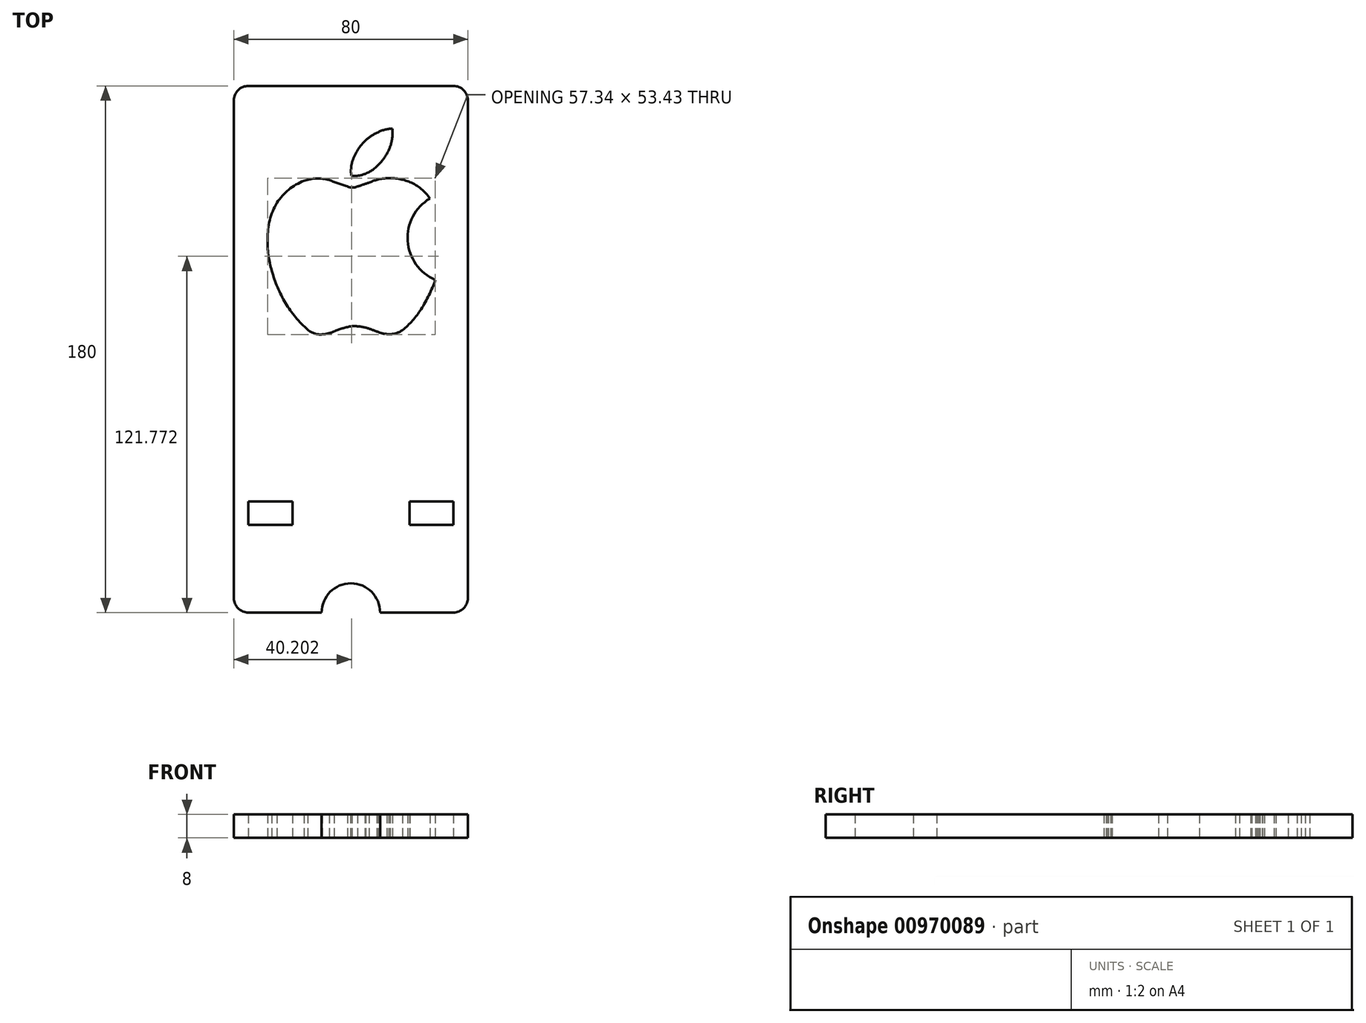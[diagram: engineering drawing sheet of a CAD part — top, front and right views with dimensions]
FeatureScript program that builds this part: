
annotation { "Feature Type Name" : "Feature", "Feature Type Description" : "" }
export const myFeature = defineFeature(function(context is Context, id is Id, definition is map)
    precondition{}
    {
        {
            var Q0;
            Q0=qCreatedBy(makeId("Top.planeOp"),FACE);
            var sketch = newSketch(context, id + "F0", { "sketchPlane" : qUnion([Q0])});
            skLineSegment(sketch, "E0.bottom", {"start": v(-35, 90) * mm, "end": v(35, 90) * mm});
            skLineSegment(sketch, "E0.top", {"start": v(-35, -90) * mm, "end": v(-10, -90) * mm});
            skLineSegment(sketch, "E0.left", {"start": v(-40, 85) * mm, "end": v(-40, -85) * mm});
            skLineSegment(sketch, "E0.right", {"start": v(40, 85) * mm, "end": v(40, -85) * mm});
            skArc(sketch, "E1", {"start": v(-10, -90) * mm, "mid": v(0, -80) * mm, "end": v(10, -90) * mm});
            skLineSegment(sketch, "E2.trimOffspring", {"start": v(10, -90) * mm, "end": v(35, -90) * mm});
            skPoint(sketch, "E3.visualSharp", {"position": v(40, 90) * mm});
            skArc(sketch, "E3.filletArc", {"start": v(40, 85) * mm, "mid": v(38.54, 88.54) * mm, "end": v(35, 90) * mm});
            skPoint(sketch, "E4.visualSharp", {"position": v(-40, 90) * mm});
            skArc(sketch, "E4.filletArc", {"start": v(-35, 90) * mm, "mid": v(-38.54, 88.54) * mm, "end": v(-40, 85) * mm});
            skPoint(sketch, "E5.visualSharp", {"position": v(40, -90) * mm});
            skArc(sketch, "E5.filletArc", {"start": v(35, -90) * mm, "mid": v(38.54, -88.54) * mm, "end": v(40, -85) * mm});
            skPoint(sketch, "E6.visualSharp", {"position": v(-40, -90) * mm});
            skArc(sketch, "E6.filletArc", {"start": v(-40, -85) * mm, "mid": v(-38.54, -88.54) * mm, "end": v(-35, -90) * mm});
            skLineSegment(sketch, "E7.bottom", {"start": v(-35, -52) * mm, "end": v(-20, -52) * mm});
            skLineSegment(sketch, "E7.top", {"start": v(-35, -60) * mm, "end": v(-20, -60) * mm});
            skLineSegment(sketch, "E7.left", {"start": v(-35, -52) * mm, "end": v(-35, -60) * mm});
            skLineSegment(sketch, "E7.right", {"start": v(-20, -52) * mm, "end": v(-20, -60) * mm});
            skLineSegment(sketch, "E8.bottom", {"start": v(20, -52) * mm, "end": v(35, -52) * mm});
            skLineSegment(sketch, "E8.top", {"start": v(20, -60) * mm, "end": v(35, -60) * mm});
            skLineSegment(sketch, "E8.left", {"start": v(20, -52) * mm, "end": v(20, -60) * mm});
            skLineSegment(sketch, "E8.right", {"start": v(35, -52) * mm, "end": v(35, -60) * mm});
            skArc(sketch, "E9", {"start": v(-16.02, 57.55) * mm, "mid": v(-21.25, 54.54) * mm, "end": v(-25.26, 50.04) * mm});
            skArc(sketch, "E10", {"start": v(-25.26, 50.04) * mm, "mid": v(-27.73, 44.1) * mm, "end": v(-28.45, 37.72) * mm});
            skArc(sketch, "E11", {"start": v(-28.45, 37.72) * mm, "mid": v(-28.19, 32.2) * mm, "end": v(-27.02, 26.8) * mm});
            skArc(sketch, "E12", {"start": v(-27.02, 26.8) * mm, "mid": v(-25.06, 21.15) * mm, "end": v(-22.35, 15.82) * mm});
            skArc(sketch, "E13", {"start": v(-22.35, 15.82) * mm, "mid": v(-18.88, 10.91) * mm, "end": v(-14.7, 6.61) * mm});
            skArc(sketch, "E14", {"start": v(-14.7, 6.61) * mm, "mid": v(-12.39, 5.35) * mm, "end": v(-9.77, 5.09) * mm});
            skArc(sketch, "E15", {"start": v(-9.77, 5.09) * mm, "mid": v(-7.7, 5.4) * mm, "end": v(-5.72, 6.08) * mm});
            skArc(sketch, "E16", {"start": v(-0.1, 7.82) * mm, "mid": v(-2.96, 7.12) * mm, "end": v(-5.72, 6.08) * mm});
            skArc(sketch, "E17", {"start": v(5.12, 7.39) * mm, "mid": v(2.53, 7.83) * mm, "end": v(-0.1, 7.82) * mm});
            skArc(sketch, "E18", {"start": v(9.36, 5.85) * mm, "mid": v(7.26, 6.67) * mm, "end": v(5.12, 7.39) * mm});
            skArc(sketch, "E19", {"start": v(9.36, 5.85) * mm, "mid": v(11.35, 5.32) * mm, "end": v(13.4, 5.14) * mm});
            skArc(sketch, "E20", {"start": v(13.4, 5.14) * mm, "mid": v(15.62, 5.52) * mm, "end": v(17.65, 6.52) * mm});
            skArc(sketch, "E21", {"start": v(17.65, 6.52) * mm, "mid": v(21.08, 9.82) * mm, "end": v(23.95, 13.62) * mm});
            skArc(sketch, "E22", {"start": v(23.95, 13.62) * mm, "mid": v(26.72, 18.52) * mm, "end": v(28.87, 23.73) * mm});
            skArc(sketch, "E23", {"start": v(27.01, 51.51) * mm, "mid": v(19.4, 37.05) * mm, "end": v(28.87, 23.73) * mm});
            skArc(sketch, "E24", {"start": v(27.01, 51.51) * mm, "mid": v(24.03, 54.81) * mm, "end": v(20.23, 57.13) * mm});
            skArc(sketch, "E25", {"start": v(20.23, 57.13) * mm, "mid": v(16.34, 58.22) * mm, "end": v(12.32, 58.47) * mm});
            skArc(sketch, "E26", {"start": v(12.32, 58.47) * mm, "mid": v(9.19, 57.98) * mm, "end": v(6.19, 56.94) * mm});
            skArc(sketch, "E27", {"start": v(2.27, 55.63) * mm, "mid": v(4.23, 56.27) * mm, "end": v(6.19, 56.94) * mm});
            skArc(sketch, "E28", {"start": v(-1.2, 55.63) * mm, "mid": v(0.53, 55.24) * mm, "end": v(2.27, 55.63) * mm});
            skArc(sketch, "E29", {"start": v(-7.41, 57.82) * mm, "mid": v(-4.33, 56.66) * mm, "end": v(-1.2, 55.63) * mm});
            skArc(sketch, "E30", {"start": v(-7.41, 57.82) * mm, "mid": v(-11.74, 58.36) * mm, "end": v(-16.02, 57.55) * mm});
            skArc(sketch, "E31", {"start": v(14.17, 75.42) * mm, "mid": v(11.45, 75) * mm, "end": v(8.9, 73.97) * mm});
            skArc(sketch, "E32", {"start": v(14.17, 72.52) * mm, "mid": v(14.2, 73.97) * mm, "end": v(14.17, 75.42) * mm});
            skArc(sketch, "E33", {"start": v(12.95, 68.05) * mm, "mid": v(13.73, 70.24) * mm, "end": v(14.17, 72.52) * mm});
            skArc(sketch, "E34", {"start": v(9.7, 63.3) * mm, "mid": v(11.5, 65.55) * mm, "end": v(12.95, 68.05) * mm});
            skArc(sketch, "E35", {"start": v(4.79, 59.9) * mm, "mid": v(7.44, 61.3) * mm, "end": v(9.7, 63.3) * mm});
            skArc(sketch, "E36", {"start": v(0.15, 59.32) * mm, "mid": v(2.5, 59.32) * mm, "end": v(4.79, 59.9) * mm});
            skArc(sketch, "E37", {"start": v(0.4, 63.85) * mm, "mid": v(0.06, 61.6) * mm, "end": v(0.15, 59.32) * mm});
            skArc(sketch, "E38", {"start": v(4.77, 71.14) * mm, "mid": v(2.12, 67.77) * mm, "end": v(0.4, 63.85) * mm});
            skArc(sketch, "E39", {"start": v(8.9, 73.97) * mm, "mid": v(6.72, 72.72) * mm, "end": v(4.77, 71.14) * mm});
            skSolve(sketch);
        }
        {
            var Q0;
            Q0=makeQuery(id+"F0.imprint","IMPRINT",FACE,{"disambiguationData":[TD([[makeQuery(id+"F0.imprint","IMPRINT",EDGE,{"derivedFrom":sQuery(id+"F0.wireOp",EDGE,"E0.bottom")}),-1.0]])]});
            extrude(context, id + "F1", {"entities" : qUnion([Q0]), "depth" : 8 * mm, "offsetDistance" : 25 * mm});
        }
    });
